# Revit family: Furniture_Table_Spacestor_Volute Breakout Table
name_source: partatom
category: Furniture
revit_build: Autodesk Revit 2015 (Build: 20140223_1515(x64)
units: mm (PartAtom-declared; Revit-internal decimal feet)

## types (29) — shared parameters
Polished Steel = Spacestor Polished Steel
Table Top = Spacestor White

## per-type parameters (varying)
| type | Circular | Height | Rectangular | Square Shaped |
| standard height bowed triangle-shaped | No | 755 mm  [stored 2.47703 ft] | No | No |
| standard height circular - 1200 DIA x 755h | Yes | 755 mm  [stored 2.47703 ft] | No | No |
| standard height square - 600w x 600d x 755h | No | 755 mm  [stored 2.47703 ft] | No | Yes |
| standard height rectangular - 1200w x 600d x 755h | No | 755 mm  [stored 2.47703 ft] | Yes | Yes |
| coffee height bowed triangle-shaped - 1100w x 1100d x 400h | No | 400 mm  [stored 1.31234 ft] | No | No |
| coffee height circular - 1000 DIA x 400h | Yes | 400 mm  [stored 1.31234 ft] | No | No |
| coffee height rectangular - 1200w x 600d x 400h | No | 400 mm  [stored 1.31234 ft] | Yes | Yes |
| coffee height square - 1000w x 1000d x 400h | No | 400 mm  [stored 1.31234 ft] | No | Yes |
| poseur height bowed triangle-shaped - 500w x 500d x 1100h | No | 1100 mm | No | No |
| poseur height circular - 400 DIA x 1100h | Yes | 1100 mm | No | No |
| poseur height rectangular - 1200w x 600d x 1100h | No | 1100 mm | Yes | Yes |
| poseur height square - 600w x 600d x 1100h | No | 1100 mm | No | Yes |
| coffee height bowed triangle-shaped - 900w x 900d x 400h | No | 400 mm  [stored 1.31234 ft] | No | No |
| coffee height circular - 1100 DIA x 400h | Yes | 400 mm  [stored 1.31234 ft] | No | No |
| coffee height circular - 900 DIA x 400h | Yes | 400 mm  [stored 1.31234 ft] | No | No |
| coffee height rectangular - 1400w x 600d x 400h | No | 400 mm  [stored 1.31234 ft] | Yes | Yes |
| coffee height square - 900w x 900d x 400h | No | 400 mm  [stored 1.31234 ft] | No | Yes |
| poseur height bowed triangle-shaped - 600w x 600d x 1100h | No | 1100 mm | No | No |
| poseur height circular - 500 DIA x 1100h | Yes | 1100 mm | No | No |
| poseur height circular - 600 DIA x 1100h | Yes | 1100 mm | No | No |
| poseur height rectangular - 1400w x 600d x 1100h | No | 1100 mm | Yes | Yes |
| poseur height square - 800w x 800d x 1100h | No | 1100 mm | No | Yes |
| standard height bowed triangle-shaped - 1200w x 1200d x 755h | No | 755 mm  [stored 2.47703 ft] | No | No |
| standard height bowed triangle-shaped - 800w x 800d x 755h | No | 755 mm  [stored 2.47703 ft] | No | No |
| standard height circular - 1400 DIA x 755h | Yes | 755 mm  [stored 2.47703 ft] | No | No |
| standard height circular - 600 DIA x 755h | Yes | 755 mm  [stored 2.47703 ft] | No | No |
| standard height circular - 800 DIA x 755h | Yes | 755 mm  [stored 2.47703 ft] | No | No |
| standard height rectangular - 1400w x 600d x 755h | No | 755 mm  [stored 2.47703 ft] | Yes | Yes |
| standard height square - 800w x 800d x 755h | No | 755 mm  [stored 2.47703 ft] | No | Yes |

note: [stored X ft] marks values corroborated as IEEE doubles in the binary element streams (Revit-internal decimal feet)

## geometry (parser evidence)
native form markers: Sweep x7
no freeform markers — native parametric forms only
